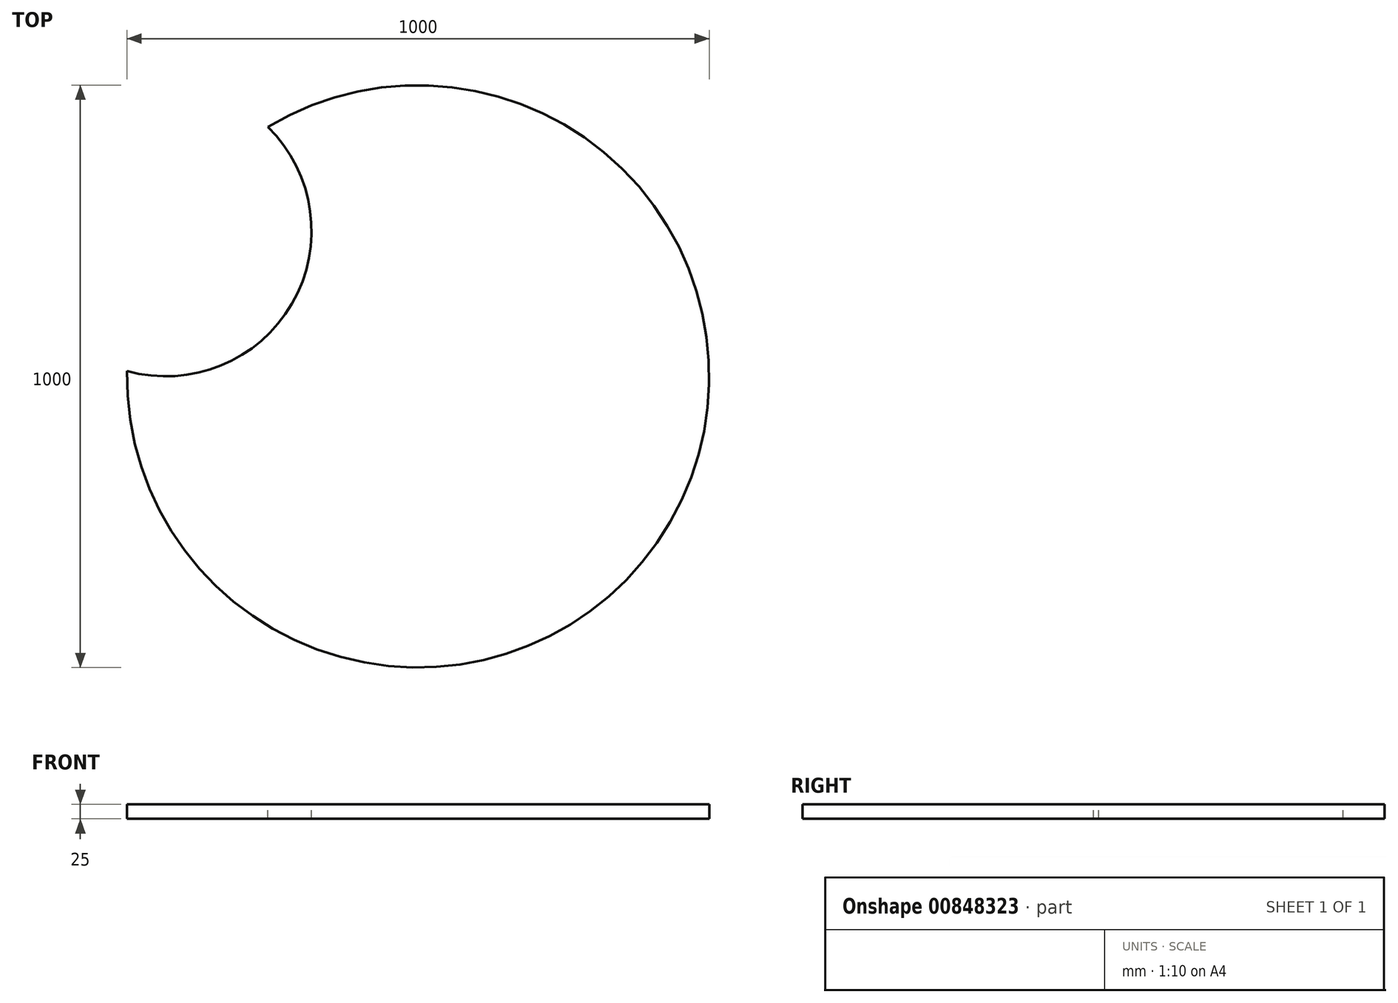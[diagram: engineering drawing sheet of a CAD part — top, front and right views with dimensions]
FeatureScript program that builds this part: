
annotation { "Feature Type Name" : "Feature", "Feature Type Description" : "" }
export const myFeature = defineFeature(function(context is Context, id is Id, definition is map)
    precondition{}
    {
        {
            var Q0;
            Q0=qCreatedBy(makeId("Top.planeOp"),FACE);
            var sketch = newSketch(context, id + "F0", { "sketchPlane" : qUnion([Q0])});
            skCircle(sketch, "E0", {"center": v(0, 0) * mm, "radius": 500 * mm});
            skSolve(sketch);
        }
        {
            var Q0;
            Q0 = qSketchRegion(id + "F0", true);
            extrude(context, id + "F1", {"entities" : qUnion([Q0]), "depth" : 25 * mm, "offsetDistance" : 25 * mm});
        }
        {
            var Q0;
            Q0=makeQuery(id+"F1.opExtrude","CAP_FACE",FACE,{"disambiguationData":[OSD([sQuery(id+"F0.wireOp",EDGE,"E0")])],"isStart":false});
            var sketch = newSketch(context, id + "F2", { "sketchPlane" : qUnion([Q0])});
            skCircle(sketch, "E1", {"center": v(-433.01, 250) * mm, "radius": 250 * mm});
            skLineSegment(sketch, "E2", {"start": v(0, 0) * mm, "end": v(-433.01, 250) * mm, "construction": true});
            skLineSegment(sketch, "E3", {"start": v(0, 0) * mm, "end": v(0, 500) * mm, "construction": true});
            skLineSegment(sketch, "E4", {"start": v(-216.5, 125) * mm, "end": v(0, 500) * mm, "construction": true});
            skSolve(sketch);
        }
        {
            var Q0;
            Q0 = qSketchRegion(id + "F2", true);
            extrude(context, id + "F3", {"entities" : qUnion([Q0]), "operationType" : NewBodyOperationType.REMOVE, "oppositeDirection" : true, "depth" : 25 * mm, "offsetDistance" : 25 * mm});
        }
    });
